# Revit family: QF_Summit_ACR1602G_24_Wide_Upright_Healthcare_Refrigerator
name_source: partatom
category: Specialty Equipment
units: mm (PartAtom-declared; Revit-internal decimal feet)

## family parameters
Always vertical = Yes
Cut with Voids When Loaded = No
Part Type = Normal
Room Calculation Point = No
Round Connector Dimension = Use Diameter
Shared = No
Work Plane-Based = No

## types (1)
- QF_Summit_ACR1602G_24_Wide_Upright_Healthcare_Refrigerator
    Apparent Power = 230 VA
    Conn Conduit = Yes
    Cycle = 60 Hz
    Default Elevation = 0 "
    Depth = 28 "
    Description = 24" Wide Upright Healthcare Refrigerator
    Elec Conn Connection Height = 0 "
    Elec Conn RI Height = 0 "
    FL Amps = 2 A
    Foodservice Equipment Identifier = Yes
    Height = 76.75 "
    Identify Quantity as Lot = Yes
    Length = 23.38 "
    Manufacturer = Summit
    Max Overcurrent Protection = 0 A
    Min Ckt Ampacity = 0 A
    Model = ACR1602G
    Number of Poles = 1
    Phase = 1
    Refrigerant Type = R600a
    Volts = 115 V
    Watts = 230 W
    Weight in Pounds = 176.4

## geometry (parser evidence)
native form markers: Blend x12, Sweep x29
no freeform markers — native parametric forms only
